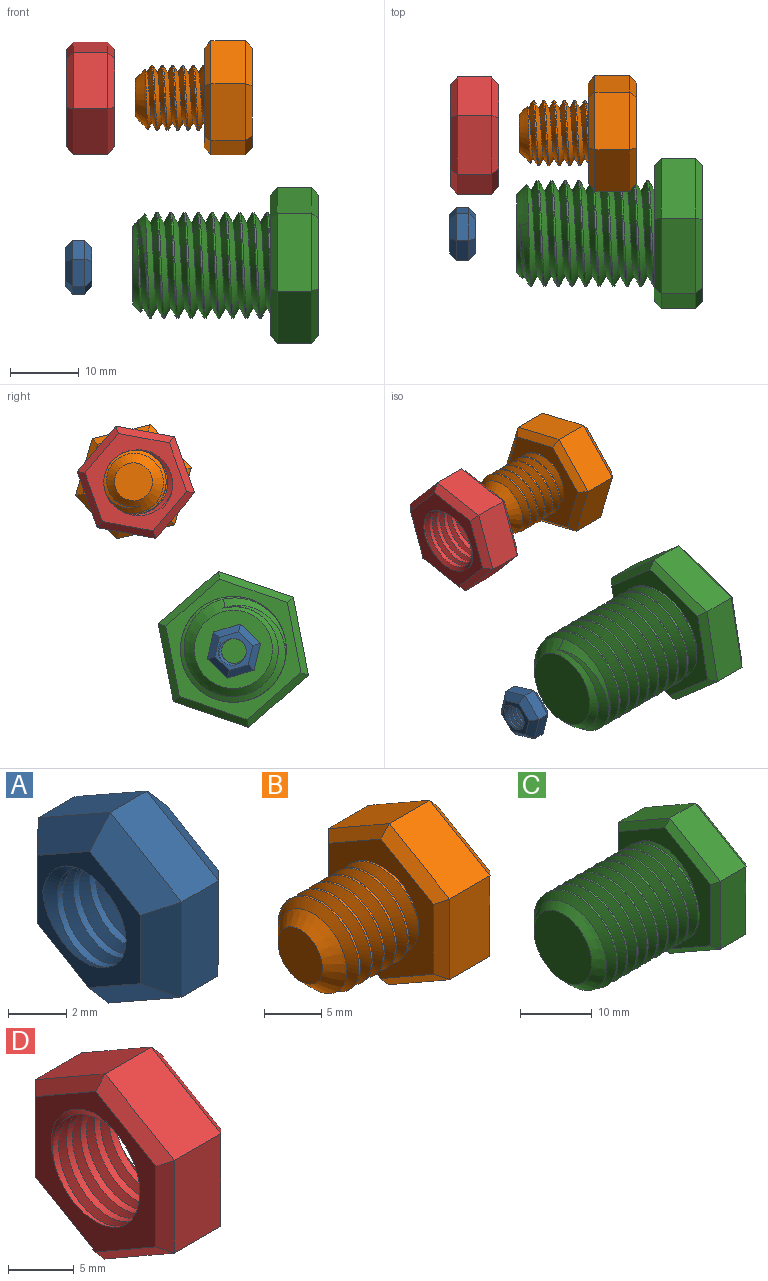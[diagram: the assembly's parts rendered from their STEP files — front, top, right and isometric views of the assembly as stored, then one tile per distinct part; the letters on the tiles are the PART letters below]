
ASSEMBLY  parts=4 mates=2
PART A: 23 faces, bbox 4.7x7.3x8.3 mm
  f0: cylinder r=1.81mm len=3.8mm, axis (1,0,0), area 15.3mm2, adj f7,f8,f21,f22
  f1: plane 3.48x2.05mm, normal (0,-0.51,0.86), area 7.3mm2, adj f2,f6,f14,f18
  f2: plane 4.04x1.8mm, normal (0,-1,-0.01), area 7.3mm2, adj f1,f3,f12,f16
  f3: plane 3.52x1.99mm, normal (0,-0.49,-0.87), area 7.3mm2, adj f2,f4,f10,f15
  f4: plane 3.48x2.05mm, normal (0,0.51,-0.86), area 7.3mm2, adj f3,f5,f9,f17
  f5: plane 4.04x1.8mm, normal (0,1,0.01), area 7.3mm2, adj f4,f6,f11,f19
  f6: plane 3.52x1.99mm, normal (0,0.49,0.87), area 7.3mm2, adj f1,f5,f13,f20
  f7: plane 6.01x5.26mm, normal (-1,0,0), area 9.6mm2, adj f0,f9,f10,f11,f12,f13,f14,f21
  f8: plane 6.01x5.26mm, normal (1,0,0), area 9.6mm2, adj f0,f15,f16,f17,f18,f19,f20,f21
  f9: plane 3.49x2.62mm, normal (-0.71,0.36,-0.61), area 4.9mm2, adj f4,f7,f10,f11
  f10: plane 3.52x2.58mm, normal (-0.71,-0.35,-0.62), area 4.9mm2, adj f3,f7,f9,f12
  f11: plane 4.04x1.03mm, normal (-0.71,0.71,0.01), area 4.9mm2, adj f5,f7,f9,f13
  f12: plane 4.04x1.03mm, normal (-0.71,-0.71,-0.01), area 4.9mm2, adj f2,f7,f10,f14
  f13: plane 3.52x2.58mm, normal (-0.71,0.35,0.62), area 4.9mm2, adj f6,f7,f11,f14
  f14: plane 3.49x2.62mm, normal (-0.71,-0.36,0.61), area 4.9mm2, adj f1,f7,f12,f13
  f15: plane 3.52x2.58mm, normal (0.71,-0.35,-0.62), area 4.9mm2, adj f3,f8,f16,f17
  f16: plane 4.04x1.03mm, normal (0.71,-0.71,-0.01), area 4.9mm2, adj f2,f8,f15,f18
  f17: plane 3.49x2.62mm, normal (0.71,0.36,-0.61), area 4.9mm2, adj f4,f8,f15,f19
  f18: plane 3.49x2.62mm, normal (0.71,-0.36,0.61), area 4.9mm2, adj f1,f8,f16,f20
  f19: plane 4.04x1.03mm, normal (0.71,0.71,0.01), area 4.9mm2, adj f5,f8,f17,f20
  f20: plane 3.52x2.58mm, normal (0.71,0.35,0.62), area 4.9mm2, adj f6,f8,f18,f19
  f21: bspline ~5.2x4.51mm, area 31.6mm2, adj f0,f7,f8,f22
  f22: bspline ~5.2x4.51mm, area 31.5mm2, adj f0,f7,f8,f21
PART B: 25 faces, bbox 17.8x15.9x18.1 mm
  f0: cylinder r=4.75mm len=9.5mm, axis (1,0,0), area 28.1mm2, adj f1,f2,f4,f12
  f1: bspline ~10.97x9.91mm, area 196.7mm2, adj f0,f2,f4,f12
  f2: bspline ~10.97x10.66mm, area 196.6mm2, adj f0,f1,f4,f12
  f3: plane 5.5x5.5mm, normal (-1,0,0), area 23.8mm2, adj f4
  f4: cone r=4.75mm half-angle=45deg, axis (1,0,0), area 47.4mm2, adj f0,f1,f2,f3
  f5: plane 7.48x5mm, normal (0,-0.5,0.86), area 43.3mm2, adj f6,f10,f18,f22
  f6: plane 8.66x5mm, normal (0,-1,0), area 43.3mm2, adj f5,f7,f16,f20
  f7: plane 7.52x5mm, normal (0,-0.5,-0.87), area 43.3mm2, adj f6,f8,f14,f19
  f8: plane 7.48x5mm, normal (0,0.5,-0.86), area 43.3mm2, adj f7,f9,f13,f21
  f9: plane 8.66x5mm, normal (0,1,0), area 43.3mm2, adj f8,f10,f15,f23
  f10: plane 7.52x5mm, normal (0,0.5,0.87), area 43.3mm2, adj f5,f9,f17,f24
  f11: plane 15.01x13.03mm, normal (1,0,0), area 146.4mm2, adj f13,f14,f15,f16,f17,f18
  f12: plane 15.83x13.85mm, normal (-1,0,0), area 89.2mm2, adj f0,f1,f2,f19,f20,f21,f22,f23
  f13: plane 7.49x4.93mm, normal (0.71,0.36,-0.61), area 11.4mm2, adj f8,f11,f14,f15
  f14: plane 7.52x4.88mm, normal (0.71,-0.35,-0.61), area 11.4mm2, adj f7,f11,f13,f16
  f15: plane 8.66x1.03mm, normal (0.71,0.71,0), area 11.4mm2, adj f9,f11,f13,f17
  f16: plane 8.66x1.03mm, normal (0.71,-0.71,0), area 11.4mm2, adj f6,f11,f14,f18
  f17: plane 7.52x4.88mm, normal (0.71,0.35,0.61), area 11.4mm2, adj f10,f11,f15,f18
  f18: plane 7.49x4.93mm, normal (0.71,-0.36,0.61), area 11.4mm2, adj f5,f11,f16,f17
  f19: plane 7.52x4.88mm, normal (-0.71,-0.35,-0.61), area 11.4mm2, adj f7,f12,f20,f21
  f20: plane 8.66x1.03mm, normal (-0.71,-0.71,0), area 11.4mm2, adj f6,f12,f19,f22
  f21: plane 7.49x4.93mm, normal (-0.71,0.36,-0.61), area 11.4mm2, adj f8,f12,f19,f23
  f22: plane 7.49x4.93mm, normal (-0.71,-0.36,0.61), area 11.4mm2, adj f5,f12,f20,f24
  f23: plane 8.66x1.03mm, normal (-0.71,0.71,0), area 11.4mm2, adj f9,f12,f21,f24
  f24: plane 7.52x4.88mm, normal (-0.71,0.35,0.61), area 11.4mm2, adj f10,f12,f22,f23
PART C: 26 faces, bbox 27.7x20x23.1 mm
  f0: cylinder r=7.68mm len=18mm, axis (1,0,0), area 139.1mm2, adj f1,f2,f5,f13
  f1: bspline ~20.88x17.74mm, area 713.8mm2, adj f0,f2,f4,f5,f13
  f2: bspline ~21.88x17.74mm, area 715.1mm2, adj f0,f1,f4,f5,f13
  f3: plane 11.36x11.36mm, normal (-1,0,0), area 101.4mm2, adj f4
  f4: cone r=7.68mm half-angle=45deg, axis (1,0,0), area 63.2mm2, adj f1,f2,f3,f5
  f5: cone r=7.68mm half-angle=45deg, axis (1,0,0), area 13.2mm2, adj f0,f1,f2,f4
  f6: plane 9.98x5.81mm, normal (0,-0.5,0.86), area 57.7mm2, adj f7,f11,f19,f23
  f7: plane 11.55x5mm, normal (0,-1,0), area 57.7mm2, adj f6,f8,f17,f21
  f8: plane 10.02x5.74mm, normal (0,-0.5,-0.87), area 57.7mm2, adj f7,f9,f15,f20
  f9: plane 9.98x5.81mm, normal (0,0.5,-0.86), area 57.7mm2, adj f8,f10,f14,f22
  f10: plane 11.55x5mm, normal (0,1,0), area 57.7mm2, adj f9,f11,f16,f24
  f11: plane 10.02x5.74mm, normal (0,0.5,0.87), area 57.7mm2, adj f6,f10,f18,f25
  f12: plane 20.78x18.04mm, normal (1,0,0), area 280.6mm2, adj f14,f15,f16,f17,f18,f19
  f13: plane 20.78x18.04mm, normal (-1,0,0), area 125.2mm2, adj f0,f1,f2,f20,f21,f22,f23,f24
  f14: plane 9.98x6.38mm, normal (0.71,0.36,-0.61), area 15.5mm2, adj f9,f12,f15,f16
  f15: plane 10.02x6.32mm, normal (0.71,-0.35,-0.61), area 15.5mm2, adj f8,f12,f14,f17
  f16: plane 11.55x1.04mm, normal (0.71,0.71,0), area 15.5mm2, adj f10,f12,f14,f18
  f17: plane 11.55x1.04mm, normal (0.71,-0.71,0), area 15.5mm2, adj f7,f12,f15,f19
  f18: plane 10.02x6.32mm, normal (0.71,0.35,0.61), area 15.5mm2, adj f11,f12,f16,f19
  f19: plane 9.98x6.38mm, normal (0.71,-0.36,0.61), area 15.5mm2, adj f6,f12,f17,f18
  f20: plane 10.02x6.32mm, normal (-0.71,-0.35,-0.61), area 15.5mm2, adj f8,f13,f21,f22
  f21: plane 11.55x1.04mm, normal (-0.71,-0.71,0), area 15.5mm2, adj f7,f13,f20,f23
  f22: plane 9.98x6.38mm, normal (-0.71,0.36,-0.61), area 15.5mm2, adj f9,f13,f20,f24
  f23: plane 9.98x6.38mm, normal (-0.71,-0.36,0.61), area 15.5mm2, adj f6,f13,f21,f25
  f24: plane 11.55x1.04mm, normal (-0.71,0.71,0), area 15.5mm2, adj f10,f13,f22,f25
  f25: plane 10.02x6.32mm, normal (-0.71,0.35,0.61), area 15.5mm2, adj f11,f13,f23,f24
PART D: 23 faces, bbox 9.1x15.4x17.7 mm
  f0: plane 7.49x5mm, normal (0,-0.5,0.86), area 43.3mm2, adj f1,f5,f13,f17
  f1: plane 8.66x5mm, normal (0,-1,0), area 43.3mm2, adj f0,f2,f11,f15
  f2: plane 7.51x5mm, normal (0,-0.5,-0.87), area 43.3mm2, adj f1,f3,f9,f14
  f3: plane 7.49x5mm, normal (0,0.5,-0.86), area 43.3mm2, adj f2,f4,f8,f16
  f4: plane 8.66x5mm, normal (0,1,0), area 43.3mm2, adj f3,f5,f10,f18
  f5: plane 7.51x5mm, normal (0,0.5,0.87), area 43.3mm2, adj f0,f4,f12,f19
  f6: plane 15.37x13.38mm, normal (-1,0,0), area 71.4mm2, adj f8,f9,f10,f11,f12,f13,f20,f21
  f7: plane 15.37x13.38mm, normal (1,0,0), area 71.4mm2, adj f14,f15,f16,f17,f18,f19,f20,f21
  f8: plane 7.49x4.93mm, normal (-0.71,0.36,-0.61), area 11.4mm2, adj f3,f6,f9,f10
  f9: plane 7.51x4.89mm, normal (-0.71,-0.35,-0.61), area 11.4mm2, adj f2,f6,f8,f11
  f10: plane 8.66x1.02mm, normal (-0.71,0.71,0), area 11.4mm2, adj f4,f6,f8,f12
  f11: plane 8.66x1.02mm, normal (-0.71,-0.71,0), area 11.4mm2, adj f1,f6,f9,f13
  f12: plane 7.51x4.89mm, normal (-0.71,0.35,0.61), area 11.4mm2, adj f5,f6,f10,f13
  f13: plane 7.49x4.93mm, normal (-0.71,-0.36,0.61), area 11.4mm2, adj f0,f6,f11,f12
  f14: plane 7.51x4.89mm, normal (0.71,-0.35,-0.61), area 11.4mm2, adj f2,f7,f15,f16
  f15: plane 8.66x1.02mm, normal (0.71,-0.71,0), area 11.4mm2, adj f1,f7,f14,f17
  f16: plane 7.49x4.93mm, normal (0.71,0.36,-0.61), area 11.4mm2, adj f3,f7,f14,f18
  f17: plane 7.49x4.93mm, normal (0.71,-0.36,0.61), area 11.4mm2, adj f0,f7,f15,f19
  f18: plane 8.66x1.02mm, normal (0.71,0.71,0), area 11.4mm2, adj f4,f7,f16,f19
  f19: plane 7.51x4.89mm, normal (0.71,0.35,0.61), area 11.4mm2, adj f5,f7,f17,f18
  f20: cylinder r=4.66mm len=9.32mm, axis (1,0,0), area 85.4mm2, adj f6,f7,f21,f22
  f21: bspline ~12.5x10.82mm, area 128.4mm2, adj f6,f7,f20,f22
  f22: bspline ~12.5x10.82mm, area 128.5mm2, adj f6,f7,f20,f21
PLACE A rot(axis=(0,0.6,-0.8),180deg) t=(-55.27,-6.86,23.48)mm fixed
PLACE B rot(axis=(-1,0,0),43.8deg) t=(-31.66,7.73,48.08)mm
PLACE C rot(axis=(1,0,0),168.8deg) t=(-22.05,-6.79,23.73)mm
PLACE D rot(axis=(1,0,0),100.2deg) t=(-48.16,7.38,48.02)mm fixed
MATE cylindrical C.f0 <-> A.f7  axis (-1,0,0) through (-45.55,-6.79,23.73)mm
MATE cylindrical B.f0 <-> D.f6  axis (-1,0,0) through (-45.16,7.73,48.08)mm
